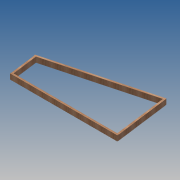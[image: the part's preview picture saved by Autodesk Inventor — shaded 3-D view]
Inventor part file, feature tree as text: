
AUTODESK INVENTOR PART (.ipt)
format: ipt  version: 2014 SP1 (Build 180222100, 222)  size: 116,736 bytes
history: native  units: in
note: dims shown in document units (in); Inventor stores cm internally (conversion verified against a paired STEP export)
features: extrude x3, sketch x3
ambient origin geometry x8: Origin, YZ Plane, XZ Plane, XY Plane, X Axis, Y Axis, Z Axis, Center Point
bodies: Body1 (feature_tree)
feature tree (6):
  extrude  "Extrusion2"  Depth=169.2913in
  extrude  "Extrusion3"  Depth=1.9685in
  extrude  "Extrusion6"  Depth=4.4882in TaperAngle=0.0deg
  sketch  "Sketch1"  dims[d0=169.2913in d1=169.2913in]
  sketch  "Sketch2"  dims[d2=165.0deg d7=1.9685in]
  sketch  "Sketch7"  dims[d11=1.4961in d12=4.4882in d13=0.0in d14=0.0394in d15=0.0in d20=0.0394in d21=0.0in]
